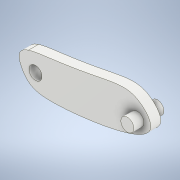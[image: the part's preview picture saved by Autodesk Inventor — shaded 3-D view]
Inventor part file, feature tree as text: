
AUTODESK INVENTOR PART (.ipt)
format: ipt  version: 2022 (Build 260153000, 153)  size: 130,560 bytes
history: native  units: in
note: dims shown in document units (in); Inventor stores cm internally (conversion verified against a paired STEP export)
features: extrude x3, sketch x2, projected_geometry x1
ambient origin geometry x8: Origin, YZ Plane, XZ Plane, XY Plane, X Axis, Y Axis, Z Axis, Center Point
bodies: Solid1 (feature_tree)
feature tree (6):
  sketch  "Sketch2"  dims[d0=0.1969in d1=0.0in d2=0.1969in d3=0.0in]
  extrude  "Extrusion1"  Depth=0.1969in TaperAngle=0.0deg
  extrude  "Extrusion2"  Depth=0.2559in
  extrude  "Extrusion3"  [1 undecoded]
  sketch  "Sketch3"  dims[d4=0.1969in d5=0.0in d6=0.2559in]
  projected_geometry  "Projected Loop2"
note: 1 required parameter value undecoded (feature->parameter linkage not recoverable at this tier; creation-order binding heuristic only, values carry confidence <= 0.55)
